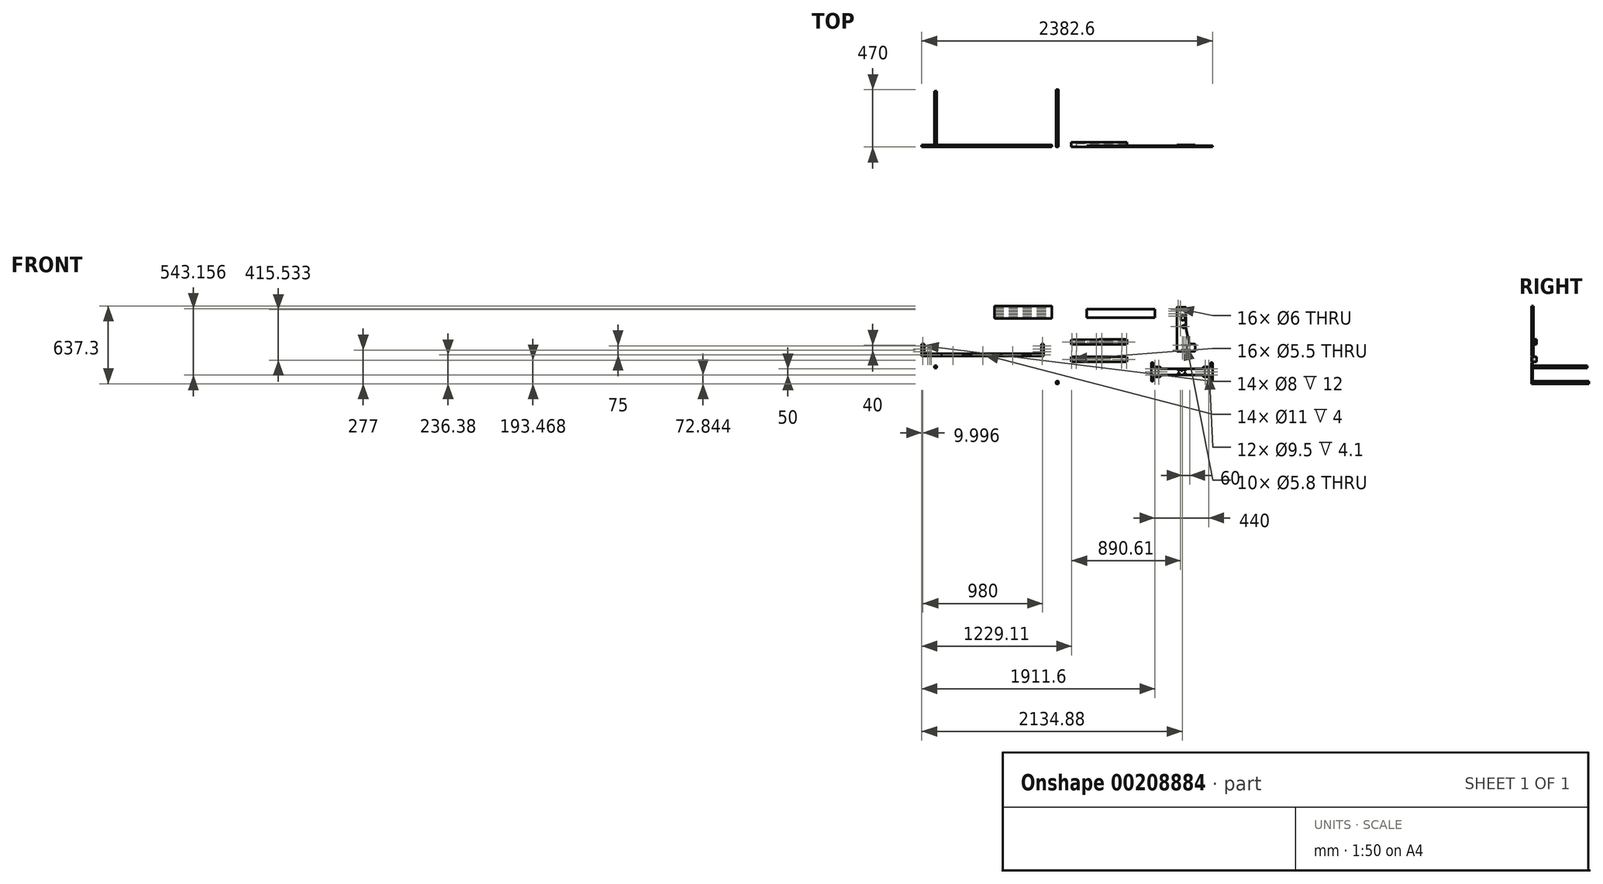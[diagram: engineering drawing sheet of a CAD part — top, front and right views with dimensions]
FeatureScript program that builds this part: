
annotation { "Feature Type Name" : "Feature", "Feature Type Description" : "" }
export const myFeature = defineFeature(function(context is Context, id is Id, definition is map)
    precondition{}
    {
        {
            var Q0;
            Q0=qCreatedBy(makeId("Front.planeOp"),FACE);
            var sketch = newSketch(context, id + "F0", { "sketchPlane" : qUnion([Q0])});
            skLineSegment(sketch, "E0.bottom", {"start": v(1.58, 127.3) * mm, "end": v(230.58, 127.3) * mm});
            skLineSegment(sketch, "E0.top", {"start": v(-227.42, 86.08) * mm, "end": v(230.58, 86.08) * mm});
            skLineSegment(sketch, "E1.0", {"start": v(225.58, 126) * mm, "end": v(225.58, 86) * mm, "construction": true});
            skLineSegment(sketch, "E2.0", {"start": v(187.58, 126) * mm, "end": v(187.58, 86) * mm, "construction": true});
            skCircle(sketch, "E3", {"center": v(187.58, 106) * mm, "radius": 2.75 * mm});
            skCircle(sketch, "E4", {"center": v(225.58, 106) * mm, "radius": 2.75 * mm});
            skLineSegment(sketch, "E5.0", {"start": v(-222.42, 126) * mm, "end": v(-222.42, 86) * mm, "construction": true});
            skLineSegment(sketch, "E6.0", {"start": v(-184.42, 126) * mm, "end": v(-184.42, 86) * mm, "construction": true});
            skCircle(sketch, "E7", {"center": v(-222.42, 106) * mm, "radius": 2.75 * mm});
            skCircle(sketch, "E8", {"center": v(-184.42, 106) * mm, "radius": 2.75 * mm});
            skLineSegment(sketch, "E9", {"start": v(1.58, 86.08) * mm, "end": v(1.58, 127.3) * mm, "construction": true});
            skLineSegment(sketch, "E10.0", {"start": v(24.58, 86) * mm, "end": v(24.58, 126) * mm, "construction": true});
            skLineSegment(sketch, "E11.0", {"start": v(-21.42, 86) * mm, "end": v(-21.42, 126) * mm, "construction": true});
            skCircle(sketch, "E12", {"center": v(24.58, 106) * mm, "radius": 3.3 * mm});
            skCircle(sketch, "E13", {"center": v(-21.42, 106) * mm, "radius": 3.3 * mm});
            skLineSegment(sketch, "E14", {"start": v(1.58, 127.3) * mm, "end": v(-227.42, 126.08) * mm});
            skLineSegment(sketch, "E15", {"start": v(-227.42, 126.08) * mm, "end": v(-227.42, 86.08) * mm});
            skLineSegment(sketch, "E16", {"start": v(230.58, 86.08) * mm, "end": v(230.58, 127.3) * mm});
            skSolve(sketch);
        }
        {
            var Q0;
            Q0=makeQuery(id+"F0.imprint","IMPRINT",FACE,{"disambiguationData":[TD([[makeQuery(id+"F0.imprint","IMPRINT",EDGE,{"derivedFrom":sQuery(id+"F0.wireOp",EDGE,"E13")}),1.0]])]});
            var Q1;
            Q1=makeQuery(id+"F0.imprint","IMPRINT",FACE,{"disambiguationData":[TD([[makeQuery(id+"F0.imprint","IMPRINT",EDGE,{"derivedFrom":sQuery(id+"F0.wireOp",EDGE,"E12")}),1.0]])]});
            var Q2;
            Q2=makeQuery(id+"F0.imprint","IMPRINT",FACE,{"disambiguationData":[TD([[makeQuery(id+"F0.imprint","IMPRINT",EDGE,{"derivedFrom":sQuery(id+"F0.wireOp",EDGE,"E8")}),1.0]])]});
            var Q3;
            Q3=makeQuery(id+"F0.imprint","IMPRINT",FACE,{"disambiguationData":[TD([[makeQuery(id+"F0.imprint","IMPRINT",EDGE,{"derivedFrom":sQuery(id+"F0.wireOp",EDGE,"E7")}),1.0]])]});
            var Q4;
            Q4=makeQuery(id+"F0.imprint","IMPRINT",FACE,{"disambiguationData":[TD([[makeQuery(id+"F0.imprint","IMPRINT",EDGE,{"derivedFrom":sQuery(id+"F0.wireOp",EDGE,"E0.bottom")}),-1.0]])]});
            var Q5;
            Q5=makeQuery(id+"F0.imprint","IMPRINT",FACE,{"disambiguationData":[TD([[makeQuery(id+"F0.imprint","IMPRINT",EDGE,{"derivedFrom":sQuery(id+"F0.wireOp",EDGE,"E3")}),1.0]])]});
            var Q6;
            Q6=makeQuery(id+"F0.imprint","IMPRINT",FACE,{"disambiguationData":[TD([[makeQuery(id+"F0.imprint","IMPRINT",EDGE,{"derivedFrom":sQuery(id+"F0.wireOp",EDGE,"E4")}),1.0]])]});
            extrude(context, id + "F1", {"entities" : qUnion([Q0, Q1, Q2, Q3, Q4, Q5, Q6]), "oppositeDirection" : true, "depth" : 40 * mm});
        }
        {
            var Q0;
            Q0=sQuery(id+"F0.wireOp",VERTEX,"E13.center");
            var Q1;
            Q1=sQuery(id+"F0.wireOp",VERTEX,"E12.center");
            var Q2;
            Q2=sQuery(id+"F0.wireOp",VERTEX,"E7.center");
            var Q3;
            Q3=sQuery(id+"F0.wireOp",VERTEX,"E8.center");
            var Q4;
            Q4=sQuery(id+"F0.wireOp",VERTEX,"E3.center");
            var Q5;
            Q5=sQuery(id+"F0.wireOp",VERTEX,"E4.center");
            var Q6;
            Q6=makeQuery(id+"F1.opExtrude","SWEPT_BODY",BODY,{"disambiguationData":[OSD([sQuery(id+"F0.wireOp",EDGE,"E0.bottom"),sQuery(id+"F0.wireOp",EDGE,"E0.top"),sQuery(id+"F0.wireOp",EDGE,"E0.left"),sQuery(id+"F0.wireOp",EDGE,"E0.right")])]});
            hole(context, id + "F2", {"style" : HoleStyle.SIMPLE, "endStyle" : HoleEndStyle.BLIND, "holeDiameter" : 5.5 * mm, "holeDepth" : 15 * mm, "locations" : qUnion([Q0, Q1, Q2, Q3, Q4, Q5]), "scope" : qUnion([Q6])});
        }
        {
            var Q0;
            Q0=makeQuery(id+"F1.opExtrude","SWEPT_FACE",FACE,{"disambiguationData":[OSD([sQuery(id+"F0.wireOp",EDGE,"E15")])]});
            var sketch = newSketch(context, id + "F3", { "sketchPlane" : qUnion([Q0])});
            skLineSegment(sketch, "E17.0", {"start": v(-20, 126.08) * mm, "end": v(-20, 86.08) * mm, "construction": true});
            skCircle(sketch, "E18", {"center": v(-30, 121.08) * mm, "radius": 3.4 * mm, "construction": true});
            skCircle(sketch, "E19.0.1.0", {"center": v(-30, 106.08) * mm, "radius": 3.4 * mm, "construction": true});
            skCircle(sketch, "E19.0.2.0", {"center": v(-30, 91.08) * mm, "radius": 3.4 * mm, "construction": true});
            skLineSegment(sketch, "E19.direction1", {"start": v(-30, 121.08) * mm, "end": v(-5, 121.08) * mm, "construction": true});
            skLineSegment(sketch, "E19.direction2", {"start": v(-30, 121.08) * mm, "end": v(-30, 106.08) * mm, "construction": true});
            skSolve(sketch);
        }
        {
            var Q0;
            Q0=sQuery(id+"F3.wireOp",VERTEX,"E18.center");
            var Q1;
            Q1=sQuery(id+"F3.wireOp",VERTEX,"E19.0.1.0.center");
            var Q2;
            Q2=sQuery(id+"F3.wireOp",VERTEX,"E19.0.2.0.center");
            var Q3;
            Q3=makeQuery(id+"F1.opExtrude","SWEPT_BODY",BODY,{"disambiguationData":[OSD([sQuery(id+"F0.wireOp",EDGE,"E0.bottom"),sQuery(id+"F0.wireOp",EDGE,"E0.top"),sQuery(id+"F0.wireOp",EDGE,"E14"),sQuery(id+"F0.wireOp",EDGE,"E15"),sQuery(id+"F0.wireOp",EDGE,"E16")])]});
            hole(context, id + "F4", {"style" : HoleStyle.SIMPLE, "endStyle" : HoleEndStyle.THROUGH, "holeDiameter" : 8 * mm, "locations" : qUnion([Q0, Q1, Q2]), "scope" : qUnion([Q3]), "isTappedThrough" : true});
        }
        {
            var Q0;
            Q0=qCreatedBy(makeId("Front.planeOp"),FACE);
            var sketch = newSketch(context, id + "F5", { "sketchPlane" : qUnion([Q0])});
            skLineSegment(sketch, "E20.bottom", {"start": v(-228.02, -16.41) * mm, "end": v(229.98, -16.41) * mm});
            skLineSegment(sketch, "E20.top", {"start": v(-228.02, -56.41) * mm, "end": v(229.98, -56.41) * mm});
            skLineSegment(sketch, "E21.0", {"start": v(224.98, -16.41) * mm, "end": v(224.98, -56.41) * mm, "construction": true});
            skLineSegment(sketch, "E22.0", {"start": v(186.98, -16.41) * mm, "end": v(186.98, -56.41) * mm, "construction": true});
            skLineSegment(sketch, "E23.0", {"start": v(-244.02, -36.41) * mm, "end": v(-185.02, -36.41) * mm, "construction": true});
            skCircle(sketch, "E24", {"center": v(186.98, -36.41) * mm, "radius": 2.75 * mm});
            skCircle(sketch, "E25", {"center": v(224.98, -36.41) * mm, "radius": 2.75 * mm});
            skLineSegment(sketch, "E26.0", {"start": v(-223.02, -16.41) * mm, "end": v(-223.02, -56.41) * mm, "construction": true});
            skLineSegment(sketch, "E27.0", {"start": v(-185.02, -16.41) * mm, "end": v(-185.02, -56.41) * mm, "construction": true});
            skCircle(sketch, "E28", {"center": v(-223.02, -36.41) * mm, "radius": 2.75 * mm});
            skCircle(sketch, "E29", {"center": v(-185.02, -36.41) * mm, "radius": 2.75 * mm});
            skLineSegment(sketch, "E30", {"start": v(0.98, -56.41) * mm, "end": v(0.98, -16.41) * mm, "construction": true});
            skLineSegment(sketch, "E31.0", {"start": v(23.98, -56.41) * mm, "end": v(23.98, -16.41) * mm, "construction": true});
            skLineSegment(sketch, "E32.0", {"start": v(-22.02, -56.41) * mm, "end": v(-22.02, -16.41) * mm, "construction": true});
            skLineSegment(sketch, "E33.trimOffspring", {"start": v(-25.32, -36.41) * mm, "end": v(27.28, -36.41) * mm, "construction": true});
            skLineSegment(sketch, "E34.trimOffspring", {"start": v(184.23, -36.41) * mm, "end": v(245.98, -36.41) * mm, "construction": true});
            skLineSegment(sketch, "E35.0", {"start": v(-25.32, -42.91) * mm, "end": v(27.28, -42.91) * mm, "construction": true});
            skLineSegment(sketch, "E36.0", {"start": v(-25.32, -29.91) * mm, "end": v(27.28, -29.91) * mm, "construction": true});
            skCircle(sketch, "E37", {"center": v(-22.02, -29.91) * mm, "radius": 3.3 * mm});
            skCircle(sketch, "E38.0.1.0", {"center": v(-22.02, -42.91) * mm, "radius": 3.3 * mm});
            skCircle(sketch, "E38.1.0.0", {"center": v(23.98, -29.91) * mm, "radius": 3.3 * mm});
            skCircle(sketch, "E38.1.1.0", {"center": v(23.98, -42.91) * mm, "radius": 3.3 * mm});
            skLineSegment(sketch, "E38.direction1", {"start": v(-22.02, -29.91) * mm, "end": v(23.98, -29.91) * mm, "construction": true});
            skLineSegment(sketch, "E38.direction2", {"start": v(-22.02, -29.91) * mm, "end": v(-22.02, -42.91) * mm, "construction": true});
            skLineSegment(sketch, "E39", {"start": v(-228.02, -16.41) * mm, "end": v(-228.02, -56.41) * mm});
            skLineSegment(sketch, "E40", {"start": v(229.98, -16.41) * mm, "end": v(229.98, -56.41) * mm});
            skSolve(sketch);
        }
        {
            var Q0;
            Q0=makeQuery(id+"F5.imprint","IMPRINT",FACE,{"disambiguationData":[TD([[makeQuery(id+"F5.imprint","IMPRINT",EDGE,{"derivedFrom":sQuery(id+"F5.wireOp",EDGE,"E38.1.1.0")}),1.0]])]});
            var Q1;
            Q1=makeQuery(id+"F5.imprint","IMPRINT",FACE,{"disambiguationData":[TD([[makeQuery(id+"F5.imprint","IMPRINT",EDGE,{"derivedFrom":sQuery(id+"F5.wireOp",EDGE,"E38.1.0.0")}),1.0]])]});
            var Q2;
            Q2=makeQuery(id+"F5.imprint","IMPRINT",FACE,{"disambiguationData":[TD([[makeQuery(id+"F5.imprint","IMPRINT",EDGE,{"derivedFrom":sQuery(id+"F5.wireOp",EDGE,"E37")}),1.0]])]});
            var Q3;
            Q3=makeQuery(id+"F5.imprint","IMPRINT",FACE,{"disambiguationData":[TD([[makeQuery(id+"F5.imprint","IMPRINT",EDGE,{"derivedFrom":sQuery(id+"F5.wireOp",EDGE,"E38.0.1.0")}),1.0]])]});
            var Q4;
            Q4=makeQuery(id+"F5.imprint","IMPRINT",FACE,{"disambiguationData":[TD([[makeQuery(id+"F5.imprint","IMPRINT",EDGE,{"derivedFrom":sQuery(id+"F5.wireOp",EDGE,"E24")}),1.0]])]});
            var Q5;
            Q5=makeQuery(id+"F5.imprint","IMPRINT",FACE,{"disambiguationData":[TD([[makeQuery(id+"F5.imprint","IMPRINT",EDGE,{"derivedFrom":sQuery(id+"F5.wireOp",EDGE,"E25")}),1.0]])]});
            var Q6;
            Q6=makeQuery(id+"F5.imprint","IMPRINT",FACE,{"disambiguationData":[TD([[makeQuery(id+"F5.imprint","IMPRINT",EDGE,{"derivedFrom":sQuery(id+"F5.wireOp",EDGE,"E29")}),1.0]])]});
            var Q7;
            Q7=makeQuery(id+"F5.imprint","IMPRINT",FACE,{"disambiguationData":[TD([[makeQuery(id+"F5.imprint","IMPRINT",EDGE,{"derivedFrom":sQuery(id+"F5.wireOp",EDGE,"E20.bottom")}),-1.0]])]});
            var Q8;
            Q8=makeQuery(id+"F5.imprint","IMPRINT",FACE,{"disambiguationData":[TD([[makeQuery(id+"F5.imprint","IMPRINT",EDGE,{"derivedFrom":sQuery(id+"F5.wireOp",EDGE,"E28")}),1.0]])]});
            extrude(context, id + "F6", {"entities" : qUnion([Q0, Q1, Q2, Q3, Q4, Q5, Q6, Q7, Q8]), "oppositeDirection" : true, "depth" : 40 * mm});
        }
        {
            var Q0;
            Q0=sQuery(id+"F5.wireOp",VERTEX,"E28.center");
            var Q1;
            Q1=sQuery(id+"F5.wireOp",VERTEX,"E23.0.end");
            var Q2;
            Q2=sQuery(id+"F5.wireOp",VERTEX,"E38.direction2.end");
            var Q3;
            Q3=sQuery(id+"F5.wireOp",VERTEX,"E37.center");
            var Q4;
            Q4=sQuery(id+"F5.wireOp",VERTEX,"E38.direction1.end");
            var Q5;
            Q5=sQuery(id+"F5.wireOp",VERTEX,"E38.1.1.0.center");
            var Q6;
            Q6=sQuery(id+"F5.wireOp",VERTEX,"E24.center");
            var Q7;
            Q7=sQuery(id+"F5.wireOp",VERTEX,"E25.center");
            var Q8;
            Q8=makeQuery(id+"F6.opExtrude","SWEPT_BODY",BODY,{"disambiguationData":[OSD([sQuery(id+"F5.wireOp",EDGE,"E20.bottom"),sQuery(id+"F5.wireOp",EDGE,"E20.top"),sQuery(id+"F5.wireOp",EDGE,"E20.left"),sQuery(id+"F5.wireOp",EDGE,"E20.right")])]});
            hole(context, id + "F7", {"style" : HoleStyle.SIMPLE, "endStyle" : HoleEndStyle.BLIND, "holeDiameter" : 5.5 * mm, "holeDepth" : 15 * mm, "locations" : qUnion([Q0, Q1, Q2, Q3, Q4, Q5, Q6, Q7]), "scope" : qUnion([Q8])});
        }
        {
            var Q0;
            Q0=qCreatedBy(makeId("Front.planeOp"),FACE);
            var sketch = newSketch(context, id + "F8", { "sketchPlane" : qUnion([Q0])});
            skLineSegment(sketch, "E41.bottom", {"start": v(-101.39, 376.02) * mm, "end": v(458.61, 376.02) * mm});
            skLineSegment(sketch, "E41.top", {"start": v(-101.39, 306.02) * mm, "end": v(458.61, 306.02) * mm});
            skLineSegment(sketch, "E41.left", {"start": v(-101.39, 376.02) * mm, "end": v(-101.39, 306.02) * mm});
            skLineSegment(sketch, "E41.right", {"start": v(458.61, 376.02) * mm, "end": v(458.61, 306.02) * mm});
            skSolve(sketch);
        }
        {
            var Q0;
            Q0=qSketchRegion(id+"F8",true);
            extrude(context, id + "F9", {"entities" : qUnion([Q0]), "oppositeDirection" : true, "depth" : 10 * mm});
        }
        {
            var Q0;
            Q0=qCreatedBy(makeId("Front.planeOp"),FACE);
            var sketch = newSketch(context, id + "F10", { "sketchPlane" : qUnion([Q0])});
            skLineSegment(sketch, "E42.bottom", {"start": v(782.75, 30.62) * mm, "end": v(642.75, 30.62) * mm});
            skLineSegment(sketch, "E42.top", {"start": v(782.75, 90.62) * mm, "end": v(762.72, 90.62) * mm});
            skLineSegment(sketch, "E42.left", {"start": v(787.75, 35.62) * mm, "end": v(787.75, 85.62) * mm});
            skLineSegment(sketch, "E42.right", {"start": v(637.75, 35.62) * mm, "end": v(637.75, 90.62) * mm});
            skLineSegment(sketch, "E43.top", {"start": v(639.25, 390.62) * mm, "end": v(711.25, 390.62) * mm});
            skLineSegment(sketch, "E43.left", {"start": v(637.75, 90.62) * mm, "end": v(637.75, 389.12) * mm});
            skLineSegment(sketch, "E43.right", {"start": v(712.75, 228.87) * mm, "end": v(712.75, 389.12) * mm});
            skLineSegment(sketch, "E44.0", {"start": v(737.75, 30.62) * mm, "end": v(737.75, 90.62) * mm, "construction": true});
            skLineSegment(sketch, "E45", {"start": v(713.25, 223.43) * mm, "end": v(733.22, 115.18) * mm});
            skPoint(sketch, "E46.trimOffspring.start.orphan", {"position": v(712.75, 61.64) * mm});
            skPoint(sketch, "E47.visualSharp", {"position": v(712.75, 226.13) * mm});
            skArc(sketch, "E47.filletArc", {"start": v(712.75, 228.87) * mm, "mid": v(712.87, 226.14) * mm, "end": v(713.25, 223.43) * mm});
            skPoint(sketch, "E48.visualSharp", {"position": v(737.75, 90.62) * mm});
            skArc(sketch, "E48.filletArc", {"start": v(733.22, 115.18) * mm, "mid": v(743.53, 97.56) * mm, "end": v(762.72, 90.62) * mm});
            skPoint(sketch, "E49.visualSharp", {"position": v(637.75, 30.62) * mm});
            skArc(sketch, "E49.filletArc", {"start": v(637.75, 35.62) * mm, "mid": v(639.21, 32.08) * mm, "end": v(642.75, 30.62) * mm});
            skPoint(sketch, "E50.visualSharp", {"position": v(787.75, 30.62) * mm});
            skArc(sketch, "E50.filletArc", {"start": v(782.75, 30.62) * mm, "mid": v(786.28, 32.08) * mm, "end": v(787.75, 35.62) * mm});
            skPoint(sketch, "E51.visualSharp", {"position": v(787.75, 90.62) * mm});
            skArc(sketch, "E51.filletArc", {"start": v(787.75, 85.62) * mm, "mid": v(786.28, 89.16) * mm, "end": v(782.75, 90.62) * mm});
            skPoint(sketch, "E52.visualSharp", {"position": v(637.75, 390.62) * mm});
            skArc(sketch, "E52.filletArc", {"start": v(639.25, 390.62) * mm, "mid": v(638.19, 390.18) * mm, "end": v(637.75, 389.12) * mm});
            skPoint(sketch, "E53.visualSharp", {"position": v(712.75, 390.62) * mm});
            skArc(sketch, "E53.filletArc", {"start": v(712.75, 389.12) * mm, "mid": v(712.3, 390.18) * mm, "end": v(711.25, 390.62) * mm});
            skLineSegment(sketch, "E54", {"start": v(712.75, 30.62) * mm, "end": v(712.75, 106.15) * mm, "construction": true});
            skLineSegment(sketch, "E55.0", {"start": v(782.75, 60.62) * mm, "end": v(642.75, 60.62) * mm, "construction": true});
            skLineSegment(sketch, "E56.bottom", {"start": v(682.75, 80.62) * mm, "end": v(742.75, 80.62) * mm, "construction": true});
            skLineSegment(sketch, "E56.top", {"start": v(682.75, 40.62) * mm, "end": v(742.75, 40.62) * mm, "construction": true});
            skLineSegment(sketch, "E56.left", {"start": v(682.75, 80.62) * mm, "end": v(682.75, 40.62) * mm, "construction": true});
            skLineSegment(sketch, "E56.right", {"start": v(742.75, 80.62) * mm, "end": v(742.75, 40.62) * mm, "construction": true});
            skPoint(sketch, "E56.middle", {"position": v(712.75, 60.62) * mm});
            skCircle(sketch, "E57", {"center": v(682.75, 80.62) * mm, "radius": 2.9 * mm, "construction": true});
            skCircle(sketch, "E58.0.1.0", {"center": v(682.75, 40.62) * mm, "radius": 2.9 * mm, "construction": true});
            skCircle(sketch, "E58.1.0.0", {"center": v(697.75, 80.62) * mm, "radius": 2.9 * mm, "construction": true});
            skCircle(sketch, "E58.1.1.0", {"center": v(697.75, 40.62) * mm, "radius": 2.9 * mm, "construction": true});
            skCircle(sketch, "E58.2.0.0", {"center": v(712.75, 80.62) * mm, "radius": 2.9 * mm, "construction": true});
            skCircle(sketch, "E58.2.1.0", {"center": v(712.75, 40.62) * mm, "radius": 2.9 * mm, "construction": true});
            skCircle(sketch, "E58.3.0.0", {"center": v(727.75, 80.62) * mm, "radius": 2.9 * mm, "construction": true});
            skCircle(sketch, "E58.3.1.0", {"center": v(727.75, 40.62) * mm, "radius": 2.9 * mm, "construction": true});
            skCircle(sketch, "E58.4.0.0", {"center": v(742.75, 80.62) * mm, "radius": 2.9 * mm, "construction": true});
            skCircle(sketch, "E58.4.1.0", {"center": v(742.75, 40.62) * mm, "radius": 2.9 * mm, "construction": true});
            skLineSegment(sketch, "E58.direction1", {"start": v(682.75, 80.62) * mm, "end": v(697.75, 80.62) * mm, "construction": true});
            skLineSegment(sketch, "E59.0", {"start": v(659.75, 90.62) * mm, "end": v(659.75, 389.12) * mm, "construction": true});
            skLineSegment(sketch, "E60.bottom", {"start": v(1072.94, 142.18) * mm, "end": v(932.94, 142.18) * mm});
            skLineSegment(sketch, "E60.top", {"start": v(1072.94, 202.18) * mm, "end": v(1053.84, 202.18) * mm});
            skLineSegment(sketch, "E60.left", {"start": v(1077.94, 147.18) * mm, "end": v(1077.94, 197.18) * mm});
            skLineSegment(sketch, "E60.right", {"start": v(927.94, 147.18) * mm, "end": v(927.94, 202.18) * mm});
            skLineSegment(sketch, "E61.top", {"start": v(929.44, 502.18) * mm, "end": v(1006.44, 502.18) * mm});
            skLineSegment(sketch, "E61.left", {"start": v(927.94, 202.18) * mm, "end": v(927.94, 500.68) * mm});
            skLineSegment(sketch, "E61.right", {"start": v(1007.94, 339.89) * mm, "end": v(1007.94, 500.68) * mm});
            skLineSegment(sketch, "E62.0", {"start": v(1027.94, 142.18) * mm, "end": v(1027.94, 202.18) * mm, "construction": true});
            skLineSegment(sketch, "E63", {"start": v(1008.26, 335.5) * mm, "end": v(1024.16, 227.8) * mm});
            skPoint(sketch, "E64.trimOffspring.start.orphan", {"position": v(1007.94, 173.2) * mm});
            skPoint(sketch, "E65.visualSharp", {"position": v(1007.94, 337.69) * mm});
            skArc(sketch, "E65.filletArc", {"start": v(1007.94, 339.89) * mm, "mid": v(1008.02, 337.7) * mm, "end": v(1008.26, 335.5) * mm});
            skPoint(sketch, "E66.visualSharp", {"position": v(1027.94, 202.18) * mm});
            skArc(sketch, "E66.filletArc", {"start": v(1024.16, 227.8) * mm, "mid": v(1034.23, 209.47) * mm, "end": v(1053.84, 202.18) * mm});
            skPoint(sketch, "E67.visualSharp", {"position": v(927.94, 142.18) * mm});
            skArc(sketch, "E67.filletArc", {"start": v(927.94, 147.18) * mm, "mid": v(929.4, 143.64) * mm, "end": v(932.94, 142.18) * mm});
            skPoint(sketch, "E68.visualSharp", {"position": v(1077.94, 142.18) * mm});
            skArc(sketch, "E68.filletArc", {"start": v(1072.94, 142.18) * mm, "mid": v(1076.47, 143.64) * mm, "end": v(1077.94, 147.18) * mm});
            skPoint(sketch, "E69.visualSharp", {"position": v(1077.94, 202.18) * mm});
            skArc(sketch, "E69.filletArc", {"start": v(1077.94, 197.18) * mm, "mid": v(1076.47, 200.71) * mm, "end": v(1072.94, 202.18) * mm});
            skPoint(sketch, "E70.visualSharp", {"position": v(927.94, 502.18) * mm});
            skArc(sketch, "E70.filletArc", {"start": v(929.44, 502.18) * mm, "mid": v(928.38, 501.74) * mm, "end": v(927.94, 500.68) * mm});
            skPoint(sketch, "E71.visualSharp", {"position": v(1007.94, 502.18) * mm});
            skArc(sketch, "E71.filletArc", {"start": v(1007.94, 500.68) * mm, "mid": v(1007.5, 501.74) * mm, "end": v(1006.44, 502.18) * mm});
            skLineSegment(sketch, "E72", {"start": v(1002.94, 142.18) * mm, "end": v(1002.94, 217.7) * mm, "construction": true});
            skLineSegment(sketch, "E73.0", {"start": v(1072.94, 172.18) * mm, "end": v(932.94, 172.18) * mm, "construction": true});
            skLineSegment(sketch, "E74.bottom", {"start": v(972.94, 192.18) * mm, "end": v(1032.94, 192.18) * mm, "construction": true});
            skLineSegment(sketch, "E74.top", {"start": v(972.94, 152.18) * mm, "end": v(1032.94, 152.18) * mm, "construction": true});
            skLineSegment(sketch, "E74.left", {"start": v(972.94, 192.18) * mm, "end": v(972.94, 152.18) * mm, "construction": true});
            skLineSegment(sketch, "E74.right", {"start": v(1032.94, 192.18) * mm, "end": v(1032.94, 152.18) * mm, "construction": true});
            skPoint(sketch, "E74.middle", {"position": v(1002.94, 172.18) * mm});
            skCircle(sketch, "E75", {"center": v(972.94, 192.18) * mm, "radius": 2.9 * mm, "construction": true});
            skCircle(sketch, "E76.0.1.0", {"center": v(972.94, 152.18) * mm, "radius": 2.9 * mm, "construction": true});
            skCircle(sketch, "E76.1.0.0", {"center": v(987.94, 192.18) * mm, "radius": 2.9 * mm, "construction": true});
            skCircle(sketch, "E76.1.1.0", {"center": v(987.94, 152.18) * mm, "radius": 2.9 * mm, "construction": true});
            skCircle(sketch, "E76.2.0.0", {"center": v(1002.94, 192.18) * mm, "radius": 2.9 * mm, "construction": true});
            skCircle(sketch, "E76.2.1.0", {"center": v(1002.94, 152.18) * mm, "radius": 2.9 * mm, "construction": true});
            skCircle(sketch, "E76.3.0.0", {"center": v(1017.94, 192.18) * mm, "radius": 2.9 * mm, "construction": true});
            skCircle(sketch, "E76.3.1.0", {"center": v(1017.94, 152.18) * mm, "radius": 2.9 * mm, "construction": true});
            skCircle(sketch, "E76.4.0.0", {"center": v(1032.94, 192.18) * mm, "radius": 2.9 * mm, "construction": true});
            skCircle(sketch, "E76.4.1.0", {"center": v(1032.94, 152.18) * mm, "radius": 2.9 * mm, "construction": true});
            skLineSegment(sketch, "E76.direction1", {"start": v(972.94, 192.18) * mm, "end": v(987.94, 192.18) * mm, "construction": true});
            skLineSegment(sketch, "E77.0", {"start": v(947.94, 202.18) * mm, "end": v(947.94, 500.68) * mm, "construction": true});
            skLineSegment(sketch, "E78.0", {"start": v(639.25, 379.62) * mm, "end": v(716.25, 379.62) * mm, "construction": true});
            skLineSegment(sketch, "E79.0", {"start": v(648.75, 90.62) * mm, "end": v(648.75, 389.12) * mm, "construction": true});
            skCircle(sketch, "E80", {"center": v(648.75, 379.62) * mm, "radius": 3 * mm});
            skLineSegment(sketch, "E81.direction1", {"start": v(648.75, 379.62) * mm, "end": v(659.75, 379.62) * mm, "construction": true});
            skCircle(sketch, "E82.0.1.0", {"center": v(648.75, 359.12) * mm, "radius": 3 * mm});
            skCircle(sketch, "E82.0.2.0", {"center": v(648.75, 338.62) * mm, "radius": 3 * mm});
            skCircle(sketch, "E82.0.3.0", {"center": v(648.75, 318.12) * mm, "radius": 3 * mm});
            skLineSegment(sketch, "E82.direction1", {"start": v(648.75, 379.62) * mm, "end": v(668.75, 379.62) * mm, "construction": true});
            skLineSegment(sketch, "E82.direction2", {"start": v(648.75, 379.62) * mm, "end": v(648.75, 359.12) * mm, "construction": true});
            skPoint(sketch, "E83.middle", {"position": v(687.75, 372.62) * mm});
            skCircle(sketch, "E84", {"center": v(687.75, 372.62) * mm, "radius": 8 * mm});
            skCircle(sketch, "E85", {"center": v(687.75, 372.62) * mm, "radius": 14 * mm});
            skLineSegment(sketch, "E86.left", {"start": v(712.75, 370.62) * mm, "end": v(712.75, 374.62) * mm});
            skLineSegment(sketch, "E86.right", {"start": v(662.75, 370.62) * mm, "end": v(662.75, 374.62) * mm});
            skCircle(sketch, "E87", {"center": v(667.56, 372.62) * mm, "radius": 2.75 * mm});
            skCircle(sketch, "E88", {"center": v(707.75, 372.62) * mm, "radius": 2.75 * mm});
            skLineSegment(sketch, "E89", {"start": v(712.75, 374.62) * mm, "end": v(694.61, 384.82) * mm});
            skLineSegment(sketch, "E90", {"start": v(712.75, 370.62) * mm, "end": v(694.61, 360.42) * mm});
            skLineSegment(sketch, "E91", {"start": v(662.75, 370.62) * mm, "end": v(680.88, 360.42) * mm});
            skLineSegment(sketch, "E92", {"start": v(662.75, 374.62) * mm, "end": v(680.88, 384.82) * mm});
            skLineSegment(sketch, "E93", {"start": v(680.88, 384.82) * mm, "end": v(680.88, 389.62) * mm});
            skLineSegment(sketch, "E94", {"start": v(694.61, 384.82) * mm, "end": v(694.61, 389.62) * mm});
            skLineSegment(sketch, "E95", {"start": v(694.61, 389.62) * mm, "end": v(680.88, 389.62) * mm});
            skPoint(sketch, "E96.middle", {"position": v(759.9, 318.54) * mm});
            skCircle(sketch, "E97", {"center": v(759.9, 318.54) * mm, "radius": 8 * mm});
            skCircle(sketch, "E98", {"center": v(759.9, 318.54) * mm, "radius": 14 * mm});
            skLineSegment(sketch, "E99.left", {"start": v(784.9, 316.54) * mm, "end": v(784.9, 320.54) * mm});
            skLineSegment(sketch, "E99.right", {"start": v(734.9, 316.54) * mm, "end": v(734.9, 320.54) * mm});
            skCircle(sketch, "E100", {"center": v(739.9, 318.54) * mm, "radius": 2.75 * mm});
            skCircle(sketch, "E101", {"center": v(779.9, 318.54) * mm, "radius": 2.75 * mm});
            skLineSegment(sketch, "E102", {"start": v(784.9, 320.54) * mm, "end": v(766.77, 330.74) * mm});
            skLineSegment(sketch, "E103", {"start": v(784.9, 316.54) * mm, "end": v(766.77, 306.34) * mm});
            skLineSegment(sketch, "E104", {"start": v(734.9, 316.54) * mm, "end": v(753.04, 306.34) * mm});
            skLineSegment(sketch, "E105", {"start": v(734.9, 320.54) * mm, "end": v(753.04, 330.74) * mm});
            skLineSegment(sketch, "E106", {"start": v(753.04, 330.74) * mm, "end": v(753.04, 335.54) * mm});
            skLineSegment(sketch, "E107", {"start": v(766.77, 330.74) * mm, "end": v(766.77, 335.54) * mm});
            skLineSegment(sketch, "E108", {"start": v(766.77, 335.54) * mm, "end": v(753.04, 335.54) * mm});
            skPoint(sketch, "E109.middle", {"position": v(687.75, 232.62) * mm});
            skCircle(sketch, "E110", {"center": v(687.75, 232.62) * mm, "radius": 8 * mm});
            skCircle(sketch, "E111", {"center": v(687.75, 232.62) * mm, "radius": 14 * mm});
            skLineSegment(sketch, "E112.left", {"start": v(712.75, 230.62) * mm, "end": v(712.75, 234.62) * mm});
            skLineSegment(sketch, "E112.right", {"start": v(662.75, 230.62) * mm, "end": v(662.75, 234.62) * mm});
            skCircle(sketch, "E113", {"center": v(667.6, 232.62) * mm, "radius": 2.75 * mm});
            skCircle(sketch, "E114", {"center": v(707.75, 232.62) * mm, "radius": 2.75 * mm});
            skLineSegment(sketch, "E115", {"start": v(712.75, 234.62) * mm, "end": v(694.61, 244.82) * mm});
            skLineSegment(sketch, "E116", {"start": v(712.75, 230.62) * mm, "end": v(694.61, 220.42) * mm});
            skLineSegment(sketch, "E117", {"start": v(662.75, 230.62) * mm, "end": v(680.88, 220.42) * mm});
            skLineSegment(sketch, "E118", {"start": v(662.75, 234.62) * mm, "end": v(680.88, 244.82) * mm});
            skLineSegment(sketch, "E119", {"start": v(680.88, 244.82) * mm, "end": v(680.88, 249.62) * mm});
            skLineSegment(sketch, "E120", {"start": v(694.61, 244.82) * mm, "end": v(694.61, 249.62) * mm});
            skLineSegment(sketch, "E121", {"start": v(694.61, 249.62) * mm, "end": v(680.88, 249.62) * mm});
            skLineSegment(sketch, "E122.bottom", {"start": v(709.75, 280.62) * mm, "end": v(665.75, 280.62) * mm});
            skLineSegment(sketch, "E122.top", {"start": v(709.75, 324.62) * mm, "end": v(665.75, 324.62) * mm});
            skLineSegment(sketch, "E122.left", {"start": v(709.75, 280.62) * mm, "end": v(709.75, 324.62) * mm});
            skLineSegment(sketch, "E122.right", {"start": v(665.75, 280.62) * mm, "end": v(665.75, 324.62) * mm});
            skPoint(sketch, "E122.middle", {"position": v(687.75, 302.62) * mm});
            skCircle(sketch, "E123", {"center": v(687.75, 302.62) * mm, "radius": 22 * mm, "construction": true});
            skLineSegment(sketch, "E124", {"start": v(709.75, 280.62) * mm, "end": v(665.75, 324.62) * mm, "construction": true});
            skLineSegment(sketch, "E125", {"start": v(665.75, 280.62) * mm, "end": v(709.75, 324.62) * mm, "construction": true});
            skCircle(sketch, "E126", {"center": v(672.2, 318.18) * mm, "radius": 4 * mm, "construction": true});
            skCircle(sketch, "E127", {"center": v(703.3, 318.18) * mm, "radius": 4 * mm, "construction": true});
            skCircle(sketch, "E128", {"center": v(703.3, 287.06) * mm, "radius": 4 * mm, "construction": true});
            skCircle(sketch, "E129", {"center": v(672.2, 287.06) * mm, "radius": 4 * mm, "construction": true});
            skCircle(sketch, "E130", {"center": v(687.75, 302.62) * mm, "radius": 18 * mm});
            skLineSegment(sketch, "E131", {"start": v(687.75, 232.62) * mm, "end": v(687.75, 390.62) * mm, "construction": true});
            skSolve(sketch);
        }
        {
            var Q0;
            Q0=makeQuery(id+"F10.imprint","IMPRINT",FACE,{"disambiguationData":[TD([[makeQuery(id+"F10.imprint","IMPRINT",EDGE,{"derivedFrom":sQuery(id+"F10.wireOp",EDGE,"E42.bottom")}),-1.0]])]});
            var Q1;
            Q1=makeQuery(id+"F10.imprint","IMPRINT",FACE,{"disambiguationData":[TD([[makeQuery(id+"F10.imprint","IMPRINT",EDGE,{"derivedFrom":sQuery(id+"F10.wireOp",EDGE,"E84")}),-1.0]])]});
            var Q2;
            Q2=makeQuery(id+"F10.imprint","IMPRINT",FACE,{"disambiguationData":[TD([[makeQuery(id+"F10.imprint","IMPRINT",EDGE,{"derivedFrom":sQuery(id+"F10.wireOp",EDGE,"E86.left")}),1.0]])]});
            var Q3;
            Q3=makeQuery(id+"F10.imprint","IMPRINT",FACE,{"disambiguationData":[TD([[makeQuery(id+"F10.imprint","IMPRINT",EDGE,{"derivedFrom":sQuery(id+"F10.wireOp",EDGE,"E86.right")}),-1.0]])]});
            var Q4;
            {var subQ2=sQuery(id+"F10.wireOp",EDGE,"E93");Q4=makeQuery(id+"F10.imprint","IMPRINT",FACE,{"disambiguationData":[TD([[makeQuery(id+"F10.imprint","IMPRINT",EDGE,{"derivedFrom":subQ2}),-1.0]])]});}
            var Q5;
            Q5=makeQuery(id+"F10.imprint","IMPRINT",FACE,{"disambiguationData":[TD([[makeQuery(id+"F10.imprint","IMPRINT",EDGE,{"derivedFrom":sQuery(id+"F10.wireOp",EDGE,"E110")}),-1.0]])]});
            var Q6;
            Q6=makeQuery(id+"F10.imprint","IMPRINT",FACE,{"disambiguationData":[TD([[makeQuery(id+"F10.imprint","IMPRINT",EDGE,{"derivedFrom":sQuery(id+"F10.wireOp",EDGE,"E112.left")}),1.0]])]});
            var Q7;
            {var subQ2=sQuery(id+"F10.wireOp",EDGE,"E119");Q7=makeQuery(id+"F10.imprint","IMPRINT",FACE,{"disambiguationData":[TD([[makeQuery(id+"F10.imprint","IMPRINT",EDGE,{"derivedFrom":subQ2}),-1.0]])]});}
            var Q8;
            Q8=makeQuery(id+"F10.imprint","IMPRINT",FACE,{"disambiguationData":[TD([[makeQuery(id+"F10.imprint","IMPRINT",EDGE,{"derivedFrom":sQuery(id+"F10.wireOp",EDGE,"E112.right")}),-1.0]])]});
            var Q9;
            Q9=makeQuery(id+"F10.imprint","IMPRINT",FACE,{"disambiguationData":[TD([[makeQuery(id+"F10.imprint","IMPRINT",EDGE,{"derivedFrom":sQuery(id+"F10.wireOp",EDGE,"E122.bottom")}),-1.0]])]});
            extrude(context, id + "F11", {"entities" : qUnion([Q0, Q1, Q2, Q3, Q4, Q5, Q6, Q7, Q8, Q9]), "oppositeDirection" : true, "depth" : 16 * mm});
        }
        {
            var Q0;
            Q0=sQuery(id+"F10.wireOp",VERTEX,"E57.center");
            var Q1;
            Q1=sQuery(id+"F10.wireOp",VERTEX,"E58.1.0.0.center");
            var Q2;
            Q2=sQuery(id+"F10.wireOp",VERTEX,"E58.2.0.0.center");
            var Q3;
            Q3=sQuery(id+"F10.wireOp",VERTEX,"E58.3.0.0.center");
            var Q4;
            Q4=sQuery(id+"F10.wireOp",VERTEX,"E56.right.start");
            var Q5;
            Q5=sQuery(id+"F10.wireOp",VERTEX,"E58.4.1.0.center");
            var Q6;
            Q6=sQuery(id+"F10.wireOp",VERTEX,"E58.3.1.0.center");
            var Q7;
            Q7=sQuery(id+"F10.wireOp",VERTEX,"E58.2.1.0.center");
            var Q8;
            Q8=sQuery(id+"F10.wireOp",VERTEX,"E58.1.1.0.center");
            var Q9;
            Q9=sQuery(id+"F10.wireOp",VERTEX,"E56.left.end");
            var Q10;
            Q10=makeQuery(id+"F11.opExtrude","SWEPT_BODY",BODY,{"disambiguationData":[OSD([sQuery(id+"F10.wireOp",EDGE,"E42.bottom"),sQuery(id+"F10.wireOp",EDGE,"E42.top"),sQuery(id+"F10.wireOp",EDGE,"E42.left"),sQuery(id+"F10.wireOp",EDGE,"E42.right"),sQuery(id+"F10.wireOp",EDGE,"E43.top"),sQuery(id+"F10.wireOp",EDGE,"E43.left"),sQuery(id+"F10.wireOp",EDGE,"E43.right"),sQuery(id+"F10.wireOp",EDGE,"E45"),sQuery(id+"F10.wireOp",EDGE,"E47.filletArc"),sQuery(id+"F10.wireOp",EDGE,"E48.filletArc"),sQuery(id+"F10.wireOp",EDGE,"E49.filletArc"),sQuery(id+"F10.wireOp",EDGE,"E50.filletArc"),sQuery(id+"F10.wireOp",EDGE,"E51.filletArc"),sQuery(id+"F10.wireOp",EDGE,"E52.filletArc"),sQuery(id+"F10.wireOp",EDGE,"E53.filletArc")])]});
            hole(context, id + "F12", {"style" : HoleStyle.SIMPLE, "endStyle" : HoleEndStyle.THROUGH, "holeDiameter" : 5.8 * mm, "locations" : qUnion([Q0, Q1, Q2, Q3, Q4, Q5, Q6, Q7, Q8, Q9]), "scope" : qUnion([Q10]), "isTappedThrough" : true});
        }
        {
            var Q0;
            Q0=sQuery(id+"F10.wireOp",VERTEX,"E127.center");
            var Q1;
            Q1=sQuery(id+"F10.wireOp",VERTEX,"E128.center");
            var Q2;
            Q2=sQuery(id+"F10.wireOp",VERTEX,"E129.center");
            var Q3;
            Q3=sQuery(id+"F10.wireOp",VERTEX,"E126.center");
            var Q4;
            Q4=makeQuery(id+"F11.opExtrude","SWEPT_BODY",BODY,{"disambiguationData":[OSD([sQuery(id+"F10.wireOp",EDGE,"E42.bottom"),sQuery(id+"F10.wireOp",EDGE,"E42.top"),sQuery(id+"F10.wireOp",EDGE,"E42.left"),sQuery(id+"F10.wireOp",EDGE,"E42.right"),sQuery(id+"F10.wireOp",EDGE,"E43.top"),sQuery(id+"F10.wireOp",EDGE,"E43.left"),sQuery(id+"F10.wireOp",EDGE,"E43.right"),sQuery(id+"F10.wireOp",EDGE,"E45"),sQuery(id+"F10.wireOp",EDGE,"E47.filletArc"),sQuery(id+"F10.wireOp",EDGE,"E48.filletArc"),sQuery(id+"F10.wireOp",EDGE,"E49.filletArc"),sQuery(id+"F10.wireOp",EDGE,"E50.filletArc"),sQuery(id+"F10.wireOp",EDGE,"E51.filletArc"),sQuery(id+"F10.wireOp",EDGE,"E52.filletArc"),sQuery(id+"F10.wireOp",EDGE,"E53.filletArc"),sQuery(id+"F10.wireOp",EDGE,"E80"),sQuery(id+"F10.wireOp",EDGE,"E82.0.1.0"),sQuery(id+"F10.wireOp",EDGE,"E82.0.2.0"),sQuery(id+"F10.wireOp",EDGE,"E82.0.3.0"),sQuery(id+"F10.wireOp",EDGE,"E82.1.0.0"),sQuery(id+"F10.wireOp",EDGE,"E82.2.0.0"),sQuery(id+"F10.wireOp",EDGE,"E82.3.0.0"),sQuery(id+"F10.wireOp",EDGE,"E84"),sQuery(id+"F10.wireOp",EDGE,"E87"),sQuery(id+"F10.wireOp",EDGE,"E88"),sQuery(id+"F10.wireOp",EDGE,"E110"),sQuery(id+"F10.wireOp",EDGE,"E113"),sQuery(id+"F10.wireOp",EDGE,"E114"),sQuery(id+"F10.wireOp",EDGE,"E130")])]});
            hole(context, id + "F13", {"style" : HoleStyle.SIMPLE, "endStyle" : HoleEndStyle.THROUGH, "holeDiameter" : 4 * mm, "locations" : qUnion([Q0, Q1, Q2, Q3]), "scope" : qUnion([Q4]), "isTappedThrough" : true});
        }
        {
            var Q0;
            Q0=qCreatedBy(makeId("Front.planeOp"),FACE);
            var sketch = newSketch(context, id + "F14", { "sketchPlane" : qUnion([Q0])});
            skLineSegment(sketch, "E132.bottom", {"start": v(444.47, -213.54) * mm, "end": v(428.47, -213.54) * mm});
            skLineSegment(sketch, "E132.top", {"start": v(444.47, -63.54) * mm, "end": v(428.47, -63.54) * mm});
            skLineSegment(sketch, "E132.left", {"start": v(444.47, -213.54) * mm, "end": v(444.47, -178.54) * mm});
            skLineSegment(sketch, "E132.right", {"start": v(428.47, -213.54) * mm, "end": v(428.47, -63.54) * mm});
            skPoint(sketch, "E132.middle", {"position": v(436.47, -138.54) * mm});
            skLineSegment(sketch, "E133", {"start": v(428.47, -138.54) * mm, "end": v(889.76, -138.54) * mm, "construction": true});
            skPoint(sketch, "E133.endSnap0", {"position": v(428.47, -138.54) * mm});
            skLineSegment(sketch, "E134.bottom", {"start": v(504.47, -178.54) * mm, "end": v(444.47, -178.54) * mm});
            skLineSegment(sketch, "E134.top", {"start": v(504.47, -98.54) * mm, "end": v(444.47, -98.54) * mm});
            skLineSegment(sketch, "E134.left", {"start": v(504.47, -178.54) * mm, "end": v(504.47, -163.54) * mm});
            skPoint(sketch, "E134.middle", {"position": v(444.47, -138.54) * mm});
            skLineSegment(sketch, "E135.trimOffspring", {"start": v(444.47, -98.54) * mm, "end": v(444.47, -63.54) * mm});
            skPoint(sketch, "E136.middle", {"position": v(504.47, -138.54) * mm});
            skLineSegment(sketch, "E137.bottom", {"start": v(679.47, -163.54) * mm, "end": v(504.47, -163.54) * mm});
            skLineSegment(sketch, "E137.top", {"start": v(679.47, -113.54) * mm, "end": v(504.47, -113.54) * mm});
            skLineSegment(sketch, "E137.left", {"start": v(679.47, -163.54) * mm, "end": v(679.47, -113.54) * mm});
            skLineSegment(sketch, "E138.trimOffspring", {"start": v(504.47, -113.54) * mm, "end": v(504.47, -98.54) * mm});
            skLineSegment(sketch, "E139", {"start": v(444.47, -98.54) * mm, "end": v(444.47, -178.54) * mm, "construction": true});
            skLineSegment(sketch, "E140.0", {"start": v(504.47, -163.54) * mm, "end": v(444.47, -163.54) * mm, "construction": true});
            skLineSegment(sketch, "E141.0", {"start": v(459.47, -98.54) * mm, "end": v(459.47, -178.54) * mm, "construction": true});
            skCircle(sketch, "E142", {"center": v(459.47, -163.54) * mm, "radius": 2.75 * mm, "construction": true});
            skCircle(sketch, "E143.0.1.0", {"center": v(459.47, -138.54) * mm, "radius": 2.75 * mm, "construction": true});
            skCircle(sketch, "E143.0.2.0", {"center": v(459.47, -113.54) * mm, "radius": 2.75 * mm, "construction": true});
            skCircle(sketch, "E143.1.0.0", {"center": v(489.47, -163.54) * mm, "radius": 2.75 * mm, "construction": true});
            skCircle(sketch, "E143.1.1.0", {"center": v(489.47, -138.54) * mm, "radius": 2.75 * mm, "construction": true});
            skCircle(sketch, "E143.1.2.0", {"center": v(489.47, -113.54) * mm, "radius": 2.75 * mm, "construction": true});
            skLineSegment(sketch, "E143.direction1", {"start": v(459.47, -163.54) * mm, "end": v(489.47, -163.54) * mm, "construction": true});
            skLineSegment(sketch, "E143.direction2", {"start": v(459.47, -163.54) * mm, "end": v(459.47, -138.54) * mm, "construction": true});
            skCircle(sketch, "E144.MirrorC", {"center": v(899.47, -163.54) * mm, "radius": 2.75 * mm, "construction": true});
            skCircle(sketch, "E145.MirrorC", {"center": v(899.47, -138.54) * mm, "radius": 2.75 * mm, "construction": true});
            skCircle(sketch, "E146.MirrorC", {"center": v(869.47, -163.54) * mm, "radius": 2.75 * mm, "construction": true});
            skPoint(sketch, "E147.MirrorP", {"position": v(854.47, -138.54) * mm});
            skCircle(sketch, "E148.MirrorC", {"center": v(869.47, -138.54) * mm, "radius": 2.75 * mm, "construction": true});
            skLineSegment(sketch, "E149.MirrorCS", {"start": v(899.47, -163.54) * mm, "end": v(899.47, -138.54) * mm, "construction": true});
            skCircle(sketch, "E150.MirrorC", {"center": v(899.47, -113.54) * mm, "radius": 2.75 * mm, "construction": true});
            skLineSegment(sketch, "E151.MirrorCS", {"start": v(899.47, -163.54) * mm, "end": v(869.47, -163.54) * mm, "construction": true});
            skCircle(sketch, "E152.MirrorC", {"center": v(869.47, -113.54) * mm, "radius": 2.75 * mm, "construction": true});
            skLineSegment(sketch, "E153.MirrorCS", {"start": v(854.47, -163.54) * mm, "end": v(914.47, -163.54) * mm, "construction": true});
            skLineSegment(sketch, "E154.MirrorCS", {"start": v(899.47, -98.54) * mm, "end": v(899.47, -178.54) * mm, "construction": true});
            skLineSegment(sketch, "E155.MirrorCS", {"start": v(914.47, -98.54) * mm, "end": v(914.47, -178.54) * mm, "construction": true});
            skPoint(sketch, "E156.MirrorP", {"position": v(930.47, -138.54) * mm});
            skLineSegment(sketch, "E157.MirrorCS", {"start": v(930.47, -213.54) * mm, "end": v(930.47, -63.54) * mm});
            skLineSegment(sketch, "E158.MirrorCS", {"start": v(854.47, -113.54) * mm, "end": v(854.47, -98.54) * mm});
            skLineSegment(sketch, "E159.MirrorCS", {"start": v(914.47, -213.54) * mm, "end": v(914.47, -178.54) * mm});
            skLineSegment(sketch, "E160.MirrorCS", {"start": v(914.47, -98.54) * mm, "end": v(914.47, -63.54) * mm});
            skLineSegment(sketch, "E161.MirrorCS", {"start": v(854.47, -178.54) * mm, "end": v(914.47, -178.54) * mm});
            skPoint(sketch, "E162.MirrorP", {"position": v(922.47, -138.54) * mm});
            skLineSegment(sketch, "E163.MirrorCS", {"start": v(854.47, -98.54) * mm, "end": v(914.47, -98.54) * mm});
            skLineSegment(sketch, "E164.MirrorCS", {"start": v(854.47, -178.54) * mm, "end": v(854.47, -163.54) * mm});
            skLineSegment(sketch, "E165.MirrorCS", {"start": v(914.47, -213.54) * mm, "end": v(930.47, -213.54) * mm});
            skLineSegment(sketch, "E166.MirrorCS", {"start": v(914.47, -63.54) * mm, "end": v(930.47, -63.54) * mm});
            skPoint(sketch, "E167.MirrorP", {"position": v(914.47, -138.54) * mm});
            skLineSegment(sketch, "E168.MirrorCS", {"start": v(679.47, -113.54) * mm, "end": v(854.47, -113.54) * mm});
            skLineSegment(sketch, "E169.MirrorCS", {"start": v(679.47, -163.54) * mm, "end": v(854.47, -163.54) * mm});
            skLineSegment(sketch, "E170.bottom", {"start": v(714.47, -163.54) * mm, "end": v(644.47, -163.54) * mm, "construction": true});
            skLineSegment(sketch, "E170.top", {"start": v(714.47, -113.54) * mm, "end": v(644.47, -113.54) * mm, "construction": true});
            skLineSegment(sketch, "E170.left", {"start": v(714.47, -163.54) * mm, "end": v(714.47, -113.54) * mm, "construction": true});
            skLineSegment(sketch, "E170.right", {"start": v(644.47, -163.54) * mm, "end": v(644.47, -113.54) * mm, "construction": true});
            skPoint(sketch, "E170.middle", {"position": v(679.47, -138.54) * mm});
            skLineSegment(sketch, "E171.0", {"start": v(714.47, -151.54) * mm, "end": v(644.47, -151.54) * mm, "construction": true});
            skLineSegment(sketch, "E172.0", {"start": v(714.47, -123.54) * mm, "end": v(644.47, -123.54) * mm, "construction": true});
            skLineSegment(sketch, "E173.0", {"start": v(654.47, -163.54) * mm, "end": v(654.47, -113.54) * mm, "construction": true});
            skCircle(sketch, "E174", {"center": v(654.47, -123.54) * mm, "radius": 3.9 * mm, "construction": true});
            skCircle(sketch, "E175.0.1.0", {"center": v(654.47, -151.54) * mm, "radius": 3.9 * mm, "construction": true});
            skCircle(sketch, "E175.1.0.0", {"center": v(679.47, -123.54) * mm, "radius": 3.9 * mm, "construction": true});
            skCircle(sketch, "E175.2.0.0", {"center": v(704.47, -123.54) * mm, "radius": 3.9 * mm, "construction": true});
            skCircle(sketch, "E175.2.1.0", {"center": v(704.47, -151.54) * mm, "radius": 3.9 * mm, "construction": true});
            skLineSegment(sketch, "E175.direction1", {"start": v(654.47, -123.54) * mm, "end": v(679.47, -123.54) * mm, "construction": true});
            skLineSegment(sketch, "E175.direction2", {"start": v(654.47, -123.54) * mm, "end": v(654.47, -151.54) * mm, "construction": true});
            skSolve(sketch);
        }
        {
            var Q0;
            Q0=qSketchRegion(id+"F14",true);
            var Q1;
            Q1=makeQuery(id+"F14.imprint","IMPRINT",FACE,{"disambiguationData":[TD([[makeQuery(id+"F14.imprint","IMPRINT",EDGE,{"derivedFrom":sQuery(id+"F14.wireOp",EDGE,"E132.bottom")}),-1.0]])]});
            var Q2;
            Q2=makeQuery(id+"F14.imprint","IMPRINT",FACE,{"disambiguationData":[TD([[makeQuery(id+"F14.imprint","IMPRINT",EDGE,{"derivedFrom":sQuery(id+"F14.wireOp",EDGE,"E137.left")}),-1.0]])]});
            extrude(context, id + "F15", {"entities" : qUnion([Q0, Q1, Q2]), "oppositeDirection" : true, "depth" : 10 * mm});
        }
        {
            var Q0;
            Q0=sQuery(id+"F14.wireOp",VERTEX,"E143.0.2.0.center");
            var Q1;
            Q1=sQuery(id+"F14.wireOp",VERTEX,"E143.1.2.0.center");
            var Q2;
            Q2=sQuery(id+"F14.wireOp",VERTEX,"E143.1.1.0.center");
            var Q3;
            Q3=sQuery(id+"F14.wireOp",VERTEX,"E143.direction1.end");
            var Q4;
            Q4=sQuery(id+"F14.wireOp",VERTEX,"E142.center");
            var Q5;
            Q5=sQuery(id+"F14.wireOp",VERTEX,"E143.direction2.end");
            var Q6;
            Q6=sQuery(id+"F14.wireOp",VERTEX,"E146.MirrorC.center");
            var Q7;
            Q7=sQuery(id+"F14.wireOp",VERTEX,"E148.MirrorC.center");
            var Q8;
            Q8=sQuery(id+"F14.wireOp",VERTEX,"E149.MirrorCS.start");
            var Q9;
            Q9=sQuery(id+"F14.wireOp",VERTEX,"E145.MirrorC.center");
            var Q10;
            Q10=sQuery(id+"F14.wireOp",VERTEX,"E152.MirrorC.center");
            var Q11;
            Q11=sQuery(id+"F14.wireOp",VERTEX,"E150.MirrorC.center");
            var Q12;
            Q12=makeQuery(id+"F15.opExtrude","SWEPT_BODY",BODY,{"disambiguationData":[OSD([sQuery(id+"F14.wireOp",EDGE,"E132.bottom"),sQuery(id+"F14.wireOp",EDGE,"E132.top"),sQuery(id+"F14.wireOp",EDGE,"E132.left"),sQuery(id+"F14.wireOp",EDGE,"E132.right"),sQuery(id+"F14.wireOp",EDGE,"E134.bottom"),sQuery(id+"F14.wireOp",EDGE,"E134.top"),sQuery(id+"F14.wireOp",EDGE,"E134.left"),sQuery(id+"F14.wireOp",EDGE,"E135.trimOffspring"),sQuery(id+"F14.wireOp",EDGE,"E137.bottom"),sQuery(id+"F14.wireOp",EDGE,"E137.top"),sQuery(id+"F14.wireOp",EDGE,"E137.left"),sQuery(id+"F14.wireOp",EDGE,"E138.trimOffspring")])]});
            hole(context, id + "F16", {"style" : HoleStyle.C_BORE, "endStyle" : HoleEndStyle.THROUGH, "holeDiameter" : 6 * mm, "cBoreDiameter" : 9.5 * mm, "cBoreDepth" : 4.1 * mm, "locations" : qUnion([Q0, Q1, Q2, Q3, Q4, Q5, Q6, Q7, Q8, Q9, Q10, Q11]), "scope" : qUnion([Q12]), "isTappedThrough" : true});
        }
        {
            var Q0;
            Q0=sQuery(id+"F14.wireOp",VERTEX,"E174.center");
            var Q1;
            Q1=sQuery(id+"F14.wireOp",VERTEX,"E175.direction1.end");
            var Q2;
            Q2=sQuery(id+"F14.wireOp",VERTEX,"E175.2.0.0.center");
            var Q3;
            Q3=sQuery(id+"F14.wireOp",VERTEX,"E175.2.1.0.center");
            var Q4;
            Q4=sQuery(id+"F14.wireOp",VERTEX,"E175.0.1.0.center");
            var Q5;
            Q5=makeQuery(id+"F15.opExtrude","SWEPT_BODY",BODY,{"disambiguationData":[OSD([sQuery(id+"F14.wireOp",EDGE,"E132.bottom"),sQuery(id+"F14.wireOp",EDGE,"E132.top"),sQuery(id+"F14.wireOp",EDGE,"E132.left"),sQuery(id+"F14.wireOp",EDGE,"E132.right"),sQuery(id+"F14.wireOp",EDGE,"E134.bottom"),sQuery(id+"F14.wireOp",EDGE,"E134.top"),sQuery(id+"F14.wireOp",EDGE,"E134.left"),sQuery(id+"F14.wireOp",EDGE,"E135.trimOffspring"),sQuery(id+"F14.wireOp",EDGE,"E137.bottom"),sQuery(id+"F14.wireOp",EDGE,"E137.top"),sQuery(id+"F14.wireOp",EDGE,"E138.trimOffspring"),sQuery(id+"F14.wireOp",EDGE,"E157.MirrorCS"),sQuery(id+"F14.wireOp",EDGE,"E158.MirrorCS"),sQuery(id+"F14.wireOp",EDGE,"E159.MirrorCS"),sQuery(id+"F14.wireOp",EDGE,"E160.MirrorCS"),sQuery(id+"F14.wireOp",EDGE,"E161.MirrorCS"),sQuery(id+"F14.wireOp",EDGE,"E163.MirrorCS"),sQuery(id+"F14.wireOp",EDGE,"E164.MirrorCS"),sQuery(id+"F14.wireOp",EDGE,"E165.MirrorCS"),sQuery(id+"F14.wireOp",EDGE,"E166.MirrorCS"),sQuery(id+"F14.wireOp",EDGE,"E168.MirrorCS"),sQuery(id+"F14.wireOp",EDGE,"E169.MirrorCS")])]});
            hole(context, id + "F17", {"style" : HoleStyle.C_BORE, "endStyle" : HoleEndStyle.BLIND, "holeDiameter" : 8 * mm, "cBoreDiameter" : 11 * mm, "cBoreDepth" : 5 * mm, "holeDepth" : 10 * mm, "locations" : qUnion([Q0, Q1, Q2, Q3, Q4]), "scope" : qUnion([Q5])});
        }
        {
            var Q0;
            Q0=makeQuery(id+"F15.opExtrude","SWEPT_EDGE",EDGE,{"disambiguationData":[OSD([sQuery(id+"F14.wireOp",EDGE,"E132.left"),sQuery(id+"F14.wireOp",EDGE,"E134.bottom")])]});
            var Q1;
            Q1=makeQuery(id+"F15.opExtrude","SWEPT_EDGE",EDGE,{"disambiguationData":[OSD([sQuery(id+"F14.wireOp",EDGE,"E134.top"),sQuery(id+"F14.wireOp",EDGE,"E135.trimOffspring")])]});
            var Q2;
            Q2=makeQuery(id+"F15.opExtrude","SWEPT_EDGE",EDGE,{"disambiguationData":[OSD([sQuery(id+"F14.wireOp",EDGE,"E137.top"),sQuery(id+"F14.wireOp",EDGE,"E138.trimOffspring")])]});
            var Q3;
            Q3=makeQuery(id+"F15.opExtrude","SWEPT_EDGE",EDGE,{"disambiguationData":[OSD([sQuery(id+"F14.wireOp",EDGE,"E134.left"),sQuery(id+"F14.wireOp",EDGE,"E137.bottom")])]});
            var Q4;
            Q4=makeQuery(id+"F15.opExtrude","SWEPT_EDGE",EDGE,{"disambiguationData":[OSD([sQuery(id+"F14.wireOp",EDGE,"E164.MirrorCS"),sQuery(id+"F14.wireOp",EDGE,"E169.MirrorCS")])]});
            var Q5;
            Q5=makeQuery(id+"F15.opExtrude","SWEPT_EDGE",EDGE,{"disambiguationData":[OSD([sQuery(id+"F14.wireOp",EDGE,"E158.MirrorCS"),sQuery(id+"F14.wireOp",EDGE,"E168.MirrorCS")])]});
            var Q6;
            Q6=makeQuery(id+"F15.opExtrude","SWEPT_EDGE",EDGE,{"disambiguationData":[OSD([sQuery(id+"F14.wireOp",EDGE,"E159.MirrorCS"),sQuery(id+"F14.wireOp",EDGE,"E161.MirrorCS")])]});
            var Q7;
            Q7=makeQuery(id+"F15.opExtrude","SWEPT_EDGE",EDGE,{"disambiguationData":[OSD([sQuery(id+"F14.wireOp",EDGE,"E160.MirrorCS"),sQuery(id+"F14.wireOp",EDGE,"E163.MirrorCS")])]});
            fillet(context, id + "F18", {"entities" : qUnion([Q0, Q1, Q2, Q3, Q4, Q5, Q6, Q7]), "radius" : 5 * mm, "tangentPropagation" : true, "allowEdgeOverflow" : false});
        }
        {
            var Q0;
            Q0=makeQuery(id+"F15.opExtrude","SWEPT_EDGE",EDGE,{"disambiguationData":[OSD([sQuery(id+"F14.wireOp",EDGE,"E159.MirrorCS"),sQuery(id+"F14.wireOp",EDGE,"E165.MirrorCS")])]});
            var Q1;
            Q1=makeQuery(id+"F15.opExtrude","SWEPT_EDGE",EDGE,{"disambiguationData":[OSD([sQuery(id+"F14.wireOp",EDGE,"E157.MirrorCS"),sQuery(id+"F14.wireOp",EDGE,"E165.MirrorCS")])]});
            var Q2;
            Q2=makeQuery(id+"F15.opExtrude","SWEPT_EDGE",EDGE,{"disambiguationData":[OSD([sQuery(id+"F14.wireOp",EDGE,"E157.MirrorCS"),sQuery(id+"F14.wireOp",EDGE,"E166.MirrorCS")])]});
            var Q3;
            Q3=makeQuery(id+"F15.opExtrude","SWEPT_EDGE",EDGE,{"disambiguationData":[OSD([sQuery(id+"F14.wireOp",EDGE,"E160.MirrorCS"),sQuery(id+"F14.wireOp",EDGE,"E166.MirrorCS")])]});
            var Q4;
            Q4=makeQuery(id+"F15.opExtrude","SWEPT_EDGE",EDGE,{"disambiguationData":[OSD([sQuery(id+"F14.wireOp",EDGE,"E158.MirrorCS"),sQuery(id+"F14.wireOp",EDGE,"E163.MirrorCS")])]});
            var Q5;
            Q5=makeQuery(id+"F15.opExtrude","SWEPT_EDGE",EDGE,{"disambiguationData":[OSD([sQuery(id+"F14.wireOp",EDGE,"E161.MirrorCS"),sQuery(id+"F14.wireOp",EDGE,"E164.MirrorCS")])]});
            var Q6;
            Q6=makeQuery(id+"F15.opExtrude","SWEPT_EDGE",EDGE,{"disambiguationData":[OSD([sQuery(id+"F14.wireOp",EDGE,"E134.bottom"),sQuery(id+"F14.wireOp",EDGE,"E134.left")])]});
            var Q7;
            Q7=makeQuery(id+"F15.opExtrude","SWEPT_EDGE",EDGE,{"disambiguationData":[OSD([sQuery(id+"F14.wireOp",EDGE,"E134.top"),sQuery(id+"F14.wireOp",EDGE,"E138.trimOffspring")])]});
            var Q8;
            Q8=makeQuery(id+"F15.opExtrude","SWEPT_EDGE",EDGE,{"disambiguationData":[OSD([sQuery(id+"F14.wireOp",EDGE,"E132.top"),sQuery(id+"F14.wireOp",EDGE,"E135.trimOffspring")])]});
            var Q9;
            Q9=makeQuery(id+"F15.opExtrude","SWEPT_EDGE",EDGE,{"disambiguationData":[OSD([sQuery(id+"F14.wireOp",EDGE,"E132.bottom"),sQuery(id+"F14.wireOp",EDGE,"E132.left")])]});
            var Q10;
            Q10=makeQuery(id+"F15.opExtrude","SWEPT_EDGE",EDGE,{"disambiguationData":[OSD([sQuery(id+"F14.wireOp",EDGE,"E132.bottom"),sQuery(id+"F14.wireOp",EDGE,"E132.right")])]});
            var Q11;
            Q11=makeQuery(id+"F15.opExtrude","SWEPT_EDGE",EDGE,{"disambiguationData":[OSD([sQuery(id+"F14.wireOp",EDGE,"E132.top"),sQuery(id+"F14.wireOp",EDGE,"E132.right")])]});
            fillet(context, id + "F19", {"entities" : qUnion([Q0, Q1, Q2, Q3, Q4, Q5, Q6, Q7, Q8, Q9, Q10, Q11]), "radius" : 3 * mm, "tangentPropagation" : true, "allowEdgeOverflow" : false});
        }
        {
            var Q0;
            Q0=qCreatedBy(makeId("Front.planeOp"),FACE);
            var sketch = newSketch(context, id + "F20", { "sketchPlane" : qUnion([Q0])});
            skLineSegment(sketch, "E176.bottom", {"start": v(-330.7, -236.38) * mm, "end": v(-350.7, -236.38) * mm});
            skLineSegment(sketch, "E176.top", {"start": v(-330.7, -216.38) * mm, "end": v(-350.7, -216.38) * mm});
            skLineSegment(sketch, "E176.left", {"start": v(-330.7, -236.38) * mm, "end": v(-330.7, -216.38) * mm});
            skLineSegment(sketch, "E176.right", {"start": v(-350.7, -236.38) * mm, "end": v(-350.7, -216.38) * mm});
            skPoint(sketch, "E176.middle", {"position": v(-340.7, -226.38) * mm});
            skCircle(sketch, "E177", {"center": v(-340.7, -226.38) * mm, "radius": 2.5 * mm});
            skSolve(sketch);
        }
        {
            var Q0;
            Q0=makeQuery(id+"F20.imprint","IMPRINT",FACE,{"disambiguationData":[TD([[makeQuery(id+"F20.imprint","IMPRINT",EDGE,{"derivedFrom":sQuery(id+"F20.wireOp",EDGE,"E176.bottom")}),-1.0]])]});
            extrude(context, id + "F21", {"entities" : qUnion([Q0]), "oppositeDirection" : true, "depth" : 470 * mm});
        }
        {
            var Q0;
            Q0=makeQuery(id+"F21.opExtrude","SWEPT_EDGE",EDGE,{"disambiguationData":[OSD([sQuery(id+"F20.wireOp",EDGE,"E176.top"),sQuery(id+"F20.wireOp",EDGE,"E176.right")])]});
            var Q1;
            Q1=makeQuery(id+"F21.opExtrude","SWEPT_EDGE",EDGE,{"disambiguationData":[OSD([sQuery(id+"F20.wireOp",EDGE,"E176.top"),sQuery(id+"F20.wireOp",EDGE,"E176.left")])]});
            var Q2;
            Q2=makeQuery(id+"F21.opExtrude","SWEPT_EDGE",EDGE,{"disambiguationData":[OSD([sQuery(id+"F20.wireOp",EDGE,"E176.bottom"),sQuery(id+"F20.wireOp",EDGE,"E176.left")])]});
            var Q3;
            Q3=makeQuery(id+"F21.opExtrude","SWEPT_EDGE",EDGE,{"disambiguationData":[OSD([sQuery(id+"F20.wireOp",EDGE,"E176.bottom"),sQuery(id+"F20.wireOp",EDGE,"E176.right")])]});
            fillet(context, id + "F22", {"entities" : qUnion([Q0, Q1, Q2, Q3]), "radius" : 3 * mm, "tangentPropagation" : true, "allowEdgeOverflow" : false});
        }
        {
            var Q0;
            Q0=qCreatedBy(makeId("Front.planeOp"),FACE);
            var sketch = newSketch(context, id + "F23", { "sketchPlane" : qUnion([Q0])});
            skLineSegment(sketch, "E178.bottom", {"start": v(-852.03, 400.92) * mm, "end": v(-388.03, 400.92) * mm});
            skLineSegment(sketch, "E178.top", {"start": v(-852.03, 300.92) * mm, "end": v(-388.03, 300.92) * mm});
            skLineSegment(sketch, "E178.left", {"start": v(-855.03, 397.92) * mm, "end": v(-855.03, 303.92) * mm});
            skLineSegment(sketch, "E178.right", {"start": v(-385.03, 397.92) * mm, "end": v(-385.03, 303.92) * mm});
            skPoint(sketch, "E179.visualSharp", {"position": v(-855.03, 400.92) * mm});
            skArc(sketch, "E179.filletArc", {"start": v(-852.03, 400.92) * mm, "mid": v(-854.15, 400.04) * mm, "end": v(-855.03, 397.92) * mm});
            skPoint(sketch, "E180.visualSharp", {"position": v(-855.03, 300.92) * mm});
            skArc(sketch, "E180.filletArc", {"start": v(-855.03, 303.92) * mm, "mid": v(-854.15, 301.8) * mm, "end": v(-852.03, 300.92) * mm});
            skPoint(sketch, "E181.visualSharp", {"position": v(-385.03, 300.92) * mm});
            skArc(sketch, "E181.filletArc", {"start": v(-388.03, 300.92) * mm, "mid": v(-385.91, 301.8) * mm, "end": v(-385.03, 303.92) * mm});
            skPoint(sketch, "E182.visualSharp", {"position": v(-385.03, 400.92) * mm});
            skArc(sketch, "E182.filletArc", {"start": v(-385.03, 397.92) * mm, "mid": v(-385.91, 400.04) * mm, "end": v(-388.03, 400.92) * mm});
            skSolve(sketch);
        }
        {
            var Q0;
            Q0=makeQuery(id+"F23.imprint","IMPRINT",FACE,{"disambiguationData":[TD([[makeQuery(id+"F23.imprint","IMPRINT",EDGE,{"derivedFrom":sQuery(id+"F23.wireOp",EDGE,"E178.bottom")}),-1.0]])]});
            extrude(context, id + "F24", {"entities" : qUnion([Q0]), "oppositeDirection" : true, "depth" : 16 * mm});
        }
        {
            var Q0;
            Q0=makeQuery(id+"F24.opExtrude","SWEPT_FACE",FACE,{"disambiguationData":[OSD([sQuery(id+"F23.wireOp",EDGE,"E178.right")])]});
            var sketch = newSketch(context, id + "F25", { "sketchPlane" : qUnion([Q0])});
            skLineSegment(sketch, "E183.0", {"start": v(16, 310.92) * mm, "end": v(0, 310.92) * mm, "construction": true});
            skCircle(sketch, "E184", {"center": v(8, 310.92) * mm, "radius": 4 * mm, "construction": true});
            skCircle(sketch, "E185.0.1.0", {"center": v(8, 335.92) * mm, "radius": 4 * mm, "construction": true});
            skCircle(sketch, "E185.0.2.0", {"center": v(8, 360.92) * mm, "radius": 4 * mm, "construction": true});
            skCircle(sketch, "E185.0.3.0", {"center": v(8, 385.92) * mm, "radius": 4 * mm, "construction": true});
            skLineSegment(sketch, "E185.direction1", {"start": v(8, 310.92) * mm, "end": v(33, 310.92) * mm, "construction": true});
            skLineSegment(sketch, "E185.direction2", {"start": v(8, 310.92) * mm, "end": v(8, 335.92) * mm, "construction": true});
            skSolve(sketch);
        }
        {
            var Q0;
            Q0=sQuery(id+"F25.wireOp",VERTEX,"E185.0.3.0.center");
            var Q1;
            Q1=sQuery(id+"F25.wireOp",VERTEX,"E185.0.2.0.center");
            var Q2;
            Q2=sQuery(id+"F25.wireOp",VERTEX,"E185.0.1.0.center");
            var Q3;
            Q3=sQuery(id+"F25.wireOp",VERTEX,"E184.center");
            var Q4;
            Q4=makeQuery(id+"F24.opExtrude","SWEPT_BODY",BODY,{"disambiguationData":[OSD([sQuery(id+"F23.wireOp",EDGE,"E178.bottom"),sQuery(id+"F23.wireOp",EDGE,"E178.top"),sQuery(id+"F23.wireOp",EDGE,"E178.left"),sQuery(id+"F23.wireOp",EDGE,"E178.right"),sQuery(id+"F23.wireOp",EDGE,"E179.filletArc"),sQuery(id+"F23.wireOp",EDGE,"E180.filletArc"),sQuery(id+"F23.wireOp",EDGE,"E181.filletArc"),sQuery(id+"F23.wireOp",EDGE,"E182.filletArc")])]});
            hole(context, id + "F26", {"style" : HoleStyle.SIMPLE, "endStyle" : HoleEndStyle.THROUGH, "holeDiameter" : 8 * mm, "locations" : qUnion([Q0, Q1, Q2, Q3]), "scope" : qUnion([Q4]), "isTappedThrough" : true});
        }
        {
            var Q0;
            Q0=qCreatedBy(makeId("Front.planeOp"),FACE);
            var sketch = newSketch(context, id + "F27", { "sketchPlane" : qUnion([Q0])});
            skLineSegment(sketch, "E186.bottom", {"start": v(-452.13, -10) * mm, "end": v(-1452.13, -10) * mm});
            skLineSegment(sketch, "E186.top", {"start": v(-472.13, 10) * mm, "end": v(-520.13, 10) * mm});
            skLineSegment(sketch, "E186.left", {"start": v(-452.13, -10) * mm, "end": v(-452.13, 10) * mm});
            skLineSegment(sketch, "E186.right", {"start": v(-1452.13, -10) * mm, "end": v(-1452.13, 10) * mm});
            skPoint(sketch, "E186.middle", {"position": v(-952.13, 0) * mm});
            skLineSegment(sketch, "E187.0", {"start": v(-462.13, 40) * mm, "end": v(-462.13, 81) * mm, "construction": true});
            skLineSegment(sketch, "E188.bottom", {"start": v(-452.13, -10) * mm, "end": v(-472.13, -10) * mm});
            skLineSegment(sketch, "E188.top", {"start": v(-452.13, 90) * mm, "end": v(-472.13, 90) * mm});
            skLineSegment(sketch, "E188.left", {"start": v(-452.13, -10) * mm, "end": v(-452.13, 90) * mm});
            skLineSegment(sketch, "E188.right", {"start": v(-472.13, 10) * mm, "end": v(-472.13, 90) * mm});
            skPoint(sketch, "E188.middle", {"position": v(-462.13, 40) * mm});
            skLineSegment(sketch, "E189.bottom", {"start": v(-1452.13, -10) * mm, "end": v(-1432.13, -10) * mm});
            skLineSegment(sketch, "E189.top", {"start": v(-1452.13, 90) * mm, "end": v(-1432.13, 90) * mm});
            skLineSegment(sketch, "E189.left", {"start": v(-1452.13, -10) * mm, "end": v(-1452.13, 90) * mm});
            skLineSegment(sketch, "E189.right", {"start": v(-1432.13, 10) * mm, "end": v(-1432.13, 90) * mm});
            skPoint(sketch, "E189.middle", {"position": v(-1442.13, 40) * mm});
            skLineSegment(sketch, "E190.0", {"start": v(-1215.94, 72.5) * mm, "end": v(-1215.94, -10) * mm, "construction": true});
            skLineSegment(sketch, "E191.bottom", {"start": v(-1198.55, -10) * mm, "end": v(-1238.55, -10) * mm});
            skPoint(sketch, "E191.middle", {"position": v(-1215.94, 10) * mm});
            skLineSegment(sketch, "E192.bottom", {"start": v(-562.13, -10) * mm, "end": v(-522.13, -10) * mm});
            skPoint(sketch, "E192.middle", {"position": v(-540.13, 10) * mm});
            skLineSegment(sketch, "E193.trimOffspring", {"start": v(-560.13, 10) * mm, "end": v(-1195.94, 10) * mm});
            skLineSegment(sketch, "E194.trimOffspring", {"start": v(-1235.94, 10) * mm, "end": v(-1432.13, 10) * mm});
            skLineSegment(sketch, "E195", {"start": v(-1195.94, 10) * mm, "end": v(-1235.94, 10) * mm});
            skPoint(sketch, "E191.left.end.orphan", {"position": v(-1193.34, 30) * mm});
            skPoint(sketch, "E191.right.end.orphan", {"position": v(-1233.34, 30) * mm});
            skLineSegment(sketch, "E196", {"start": v(-520.13, 10) * mm, "end": v(-560.13, 10) * mm});
            skCircle(sketch, "E197", {"center": v(-952.13, 0) * mm, "radius": 5.5 * mm, "construction": true});
            skCircle(sketch, "E198.1.0.0", {"center": v(-707.13, 0) * mm, "radius": 5.5 * mm, "construction": true});
            skCircle(sketch, "E198.2.0.0", {"center": v(-462.13, 0) * mm, "radius": 5.5 * mm, "construction": true});
            skLineSegment(sketch, "E198.direction1", {"start": v(-952.13, 0) * mm, "end": v(-707.13, 0) * mm, "construction": true});
            skLineSegment(sketch, "E199", {"start": v(-452.13, 10) * mm, "end": v(-472.13, -10) * mm, "construction": true});
            skLineSegment(sketch, "E200", {"start": v(-472.13, 10) * mm, "end": v(-452.13, -10) * mm, "construction": true});
            skCircle(sketch, "E201.1.0.0", {"center": v(-1197.13, 0) * mm, "radius": 5.5 * mm, "construction": true});
            skCircle(sketch, "E201.2.0.0", {"center": v(-1442.13, 0) * mm, "radius": 5.5 * mm, "construction": true});
            skLineSegment(sketch, "E201.direction1", {"start": v(-952.13, 0) * mm, "end": v(-1197.13, 0) * mm, "construction": true});
            skCircle(sketch, "E202.0.1.0", {"center": v(-462.13, 25) * mm, "radius": 5.5 * mm, "construction": true});
            skCircle(sketch, "E202.0.2.0", {"center": v(-462.13, 50) * mm, "radius": 5.5 * mm, "construction": true});
            skCircle(sketch, "E202.0.3.0", {"center": v(-462.13, 75) * mm, "radius": 5.5 * mm, "construction": true});
            skLineSegment(sketch, "E202.direction1", {"start": v(-467.13, 0) * mm, "end": v(-462.13, 0) * mm, "construction": true});
            skLineSegment(sketch, "E202.direction2", {"start": v(-462.13, 0) * mm, "end": v(-462.13, 25) * mm, "construction": true});
            skCircle(sketch, "E203.0.1.0", {"center": v(-1442.13, 25) * mm, "radius": 5.5 * mm, "construction": true});
            skCircle(sketch, "E203.0.2.0", {"center": v(-1442.13, 50) * mm, "radius": 5.5 * mm, "construction": true});
            skCircle(sketch, "E203.0.3.0", {"center": v(-1442.13, 75) * mm, "radius": 5.5 * mm, "construction": true});
            skLineSegment(sketch, "E203.direction1", {"start": v(-1442.13, 0) * mm, "end": v(-1387.13, 0) * mm, "construction": true});
            skLineSegment(sketch, "E203.direction2", {"start": v(-1442.13, 0) * mm, "end": v(-1442.13, 25) * mm, "construction": true});
            skLineSegment(sketch, "E204", {"start": v(-1402.13, 10) * mm, "end": v(-1402.13, -10) * mm, "construction": true});
            skCircle(sketch, "E205", {"center": v(-1402.13, 0) * mm, "radius": 4 * mm, "construction": true});
            skCircle(sketch, "E206.1.0.0", {"center": v(-1387.13, 0) * mm, "radius": 4 * mm, "construction": true});
            skCircle(sketch, "E206.2.0.0", {"center": v(-1372.13, 0) * mm, "radius": 4 * mm, "construction": true});
            skLineSegment(sketch, "E206.direction1", {"start": v(-1402.13, 0) * mm, "end": v(-1387.13, 0) * mm, "construction": true});
            skSolve(sketch);
        }
        {
            var Q0;
            Q0=qSketchRegion(id+"F27",true);
            extrude(context, id + "F28", {"entities" : qUnion([Q0]), "oppositeDirection" : true, "depth" : 16 * mm});
        }
        {
            var Q0;
            Q0=sQuery(id+"F27.wireOp",VERTEX,"E201.2.0.0.center");
            var Q1;
            Q1=sQuery(id+"F27.wireOp",VERTEX,"E203.direction2.end");
            var Q2;
            Q2=sQuery(id+"F27.wireOp",VERTEX,"E203.0.2.0.center");
            var Q3;
            Q3=sQuery(id+"F27.wireOp",VERTEX,"E203.0.3.0.center");
            var Q4;
            Q4=sQuery(id+"F27.wireOp",VERTEX,"E201.direction1.end");
            var Q5;
            Q5=sQuery(id+"F27.wireOp",VERTEX,"E186.middle");
            var Q6;
            Q6=sQuery(id+"F27.wireOp",VERTEX,"E198.1.0.0.center");
            var Q7;
            Q7=sQuery(id+"F27.wireOp",VERTEX,"E202.direction1.start");
            var Q8;
            Q8=sQuery(id+"F27.wireOp",VERTEX,"E202.direction2.end");
            var Q9;
            Q9=sQuery(id+"F27.wireOp",VERTEX,"E202.0.2.0.center");
            var Q10;
            Q10=sQuery(id+"F27.wireOp",VERTEX,"E202.0.3.0.center");
            var Q11;
            Q11=sQuery(id+"F27.wireOp",VERTEX,"E206.1.0.0.center");
            var Q12;
            Q12=sQuery(id+"F27.wireOp",VERTEX,"E206.2.0.0.center");
            var Q13;
            Q13=sQuery(id+"F27.wireOp",VERTEX,"E206.direction1.start");
            var Q14;
            Q14=makeQuery(id+"F28.opExtrude","SWEPT_BODY",BODY,{"disambiguationData":[OSD([sQuery(id+"F27.wireOp",EDGE,"E186.bottom"),sQuery(id+"F27.wireOp",EDGE,"E186.top"),sQuery(id+"F27.wireOp",EDGE,"E188.bottom"),sQuery(id+"F27.wireOp",EDGE,"E188.top"),sQuery(id+"F27.wireOp",EDGE,"E188.left"),sQuery(id+"F27.wireOp",EDGE,"E188.right"),sQuery(id+"F27.wireOp",EDGE,"E189.bottom"),sQuery(id+"F27.wireOp",EDGE,"E189.top"),sQuery(id+"F27.wireOp",EDGE,"E189.left"),sQuery(id+"F27.wireOp",EDGE,"E189.right"),sQuery(id+"F27.wireOp",EDGE,"E191.bottom"),sQuery(id+"F27.wireOp",EDGE,"E192.bottom"),sQuery(id+"F27.wireOp",EDGE,"E193.trimOffspring"),sQuery(id+"F27.wireOp",EDGE,"E194.trimOffspring"),sQuery(id+"F27.wireOp",EDGE,"E195"),sQuery(id+"F27.wireOp",EDGE,"E196")])]});
            hole(context, id + "F29", {"style" : HoleStyle.C_BORE, "endStyle" : HoleEndStyle.THROUGH, "holeDiameter" : 8 * mm, "cBoreDiameter" : 11 * mm, "cBoreDepth" : 4 * mm, "locations" : qUnion([Q0, Q1, Q2, Q3, Q4, Q5, Q6, Q7, Q8, Q9, Q10, Q11, Q12, Q13]), "scope" : qUnion([Q14]), "isTappedThrough" : true});
        }
        {
            var Q0;
            Q0=qCreatedBy(makeId("Front.planeOp"),FACE);
            var sketch = newSketch(context, id + "F30", { "sketchPlane" : qUnion([Q0])});
            skLineSegment(sketch, "E207.bottom", {"start": v(-1329.5, -106.63) * mm, "end": v(-1349.5, -106.63) * mm});
            skLineSegment(sketch, "E207.top", {"start": v(-1329.5, -86.63) * mm, "end": v(-1349.5, -86.63) * mm});
            skLineSegment(sketch, "E207.left", {"start": v(-1329.5, -106.63) * mm, "end": v(-1329.5, -86.63) * mm});
            skLineSegment(sketch, "E207.right", {"start": v(-1349.5, -106.63) * mm, "end": v(-1349.5, -86.63) * mm});
            skPoint(sketch, "E207.middle", {"position": v(-1339.5, -96.63) * mm});
            skCircle(sketch, "E208", {"center": v(-1339.5, -96.63) * mm, "radius": 4 * mm});
            skSolve(sketch);
        }
        {
            var Q0;
            Q0=makeQuery(id+"F30.imprint","IMPRINT",FACE,{"disambiguationData":[TD([[makeQuery(id+"F30.imprint","IMPRINT",EDGE,{"derivedFrom":sQuery(id+"F30.wireOp",EDGE,"E207.bottom")}),-1.0]])]});
            extrude(context, id + "F31", {"entities" : qUnion([Q0]), "oppositeDirection" : true, "depth" : 458 * mm});
        }
    });
